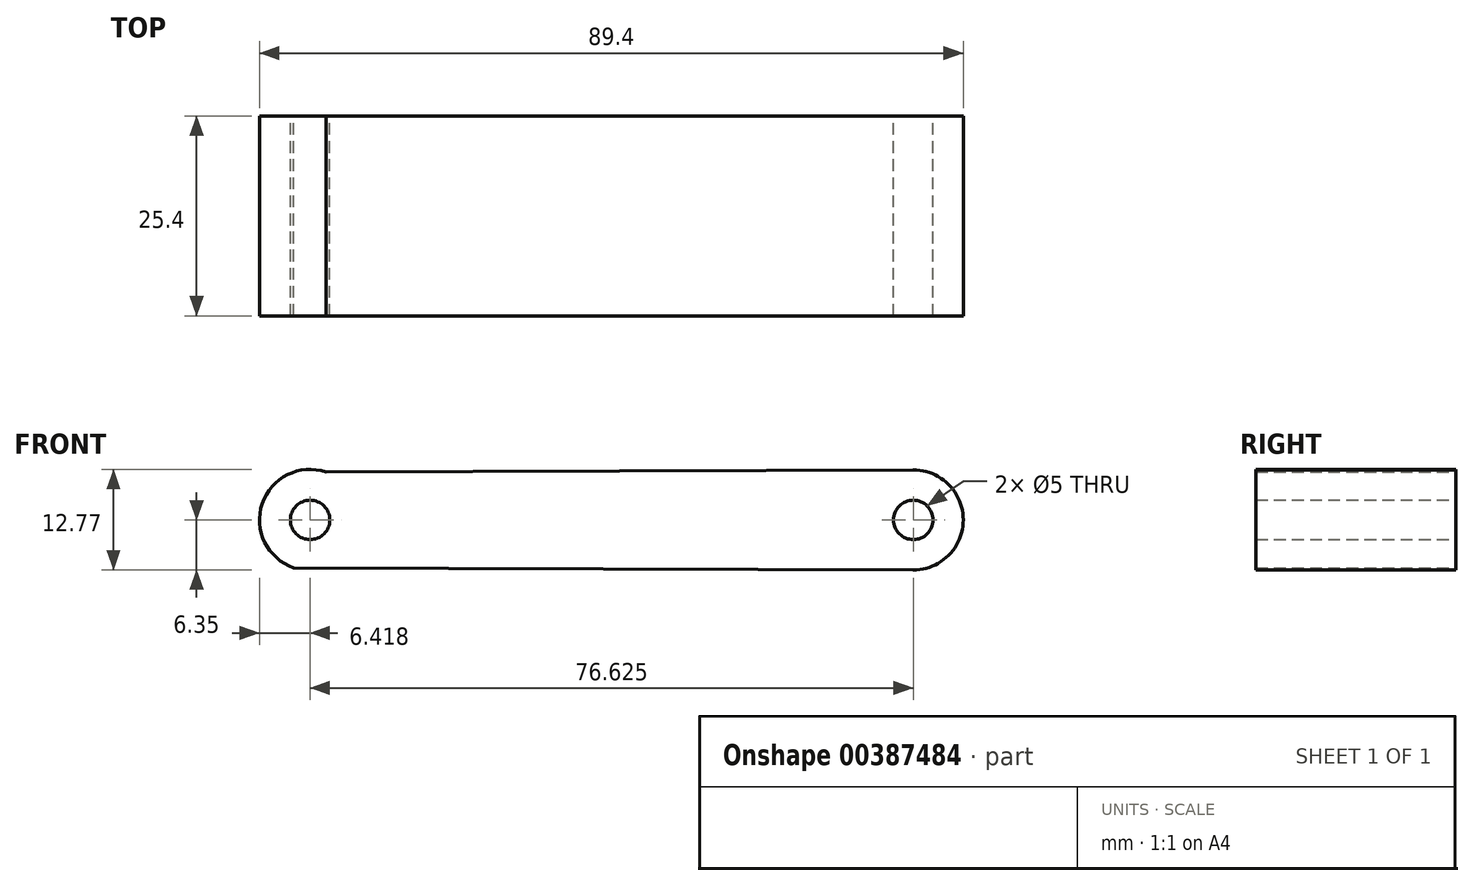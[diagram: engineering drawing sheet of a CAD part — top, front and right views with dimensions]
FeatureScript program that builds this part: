
annotation { "Feature Type Name" : "Feature", "Feature Type Description" : "" }
export const myFeature = defineFeature(function(context is Context, id is Id, definition is map)
    precondition{}
    {
        {
            var Q0;
            Q0=qCreatedBy(makeId("Front.planeOp"),FACE);
            var sketch = newSketch(context, id + "F0", { "sketchPlane" : qUnion([Q0])});
            skCircle(sketch, "E0", {"center": v(-36.06, 0) * mm, "radius": 2.5 * mm});
            skCircle(sketch, "E1", {"center": v(40.56, 0) * mm, "radius": 2.5 * mm});
            skArc(sketch, "E2", {"start": v(-34.03, 6.09) * mm, "mid": v(-42.14, 2.05) * mm, "end": v(-38.14, -6.07) * mm});
            skArc(sketch, "E3", {"start": v(40.54, -6.35) * mm, "mid": v(46.92, 0) * mm, "end": v(40.54, 6.35) * mm});
            skLineSegment(sketch, "E4", {"start": v(-38.14, -6.07) * mm, "end": v(42.08, -6.36) * mm});
            skLineSegment(sketch, "E5", {"start": v(-38.14, 6.07) * mm, "end": v(42.08, 6.36) * mm});
            skSolve(sketch);
        }
        {
            var Q0;
            Q0=qSketchRegion(id+"F0",true);
            extrude(context, id + "F1", {"entities" : qUnion([Q0]), "depth" : 25.4 * mm});
        }
    });
